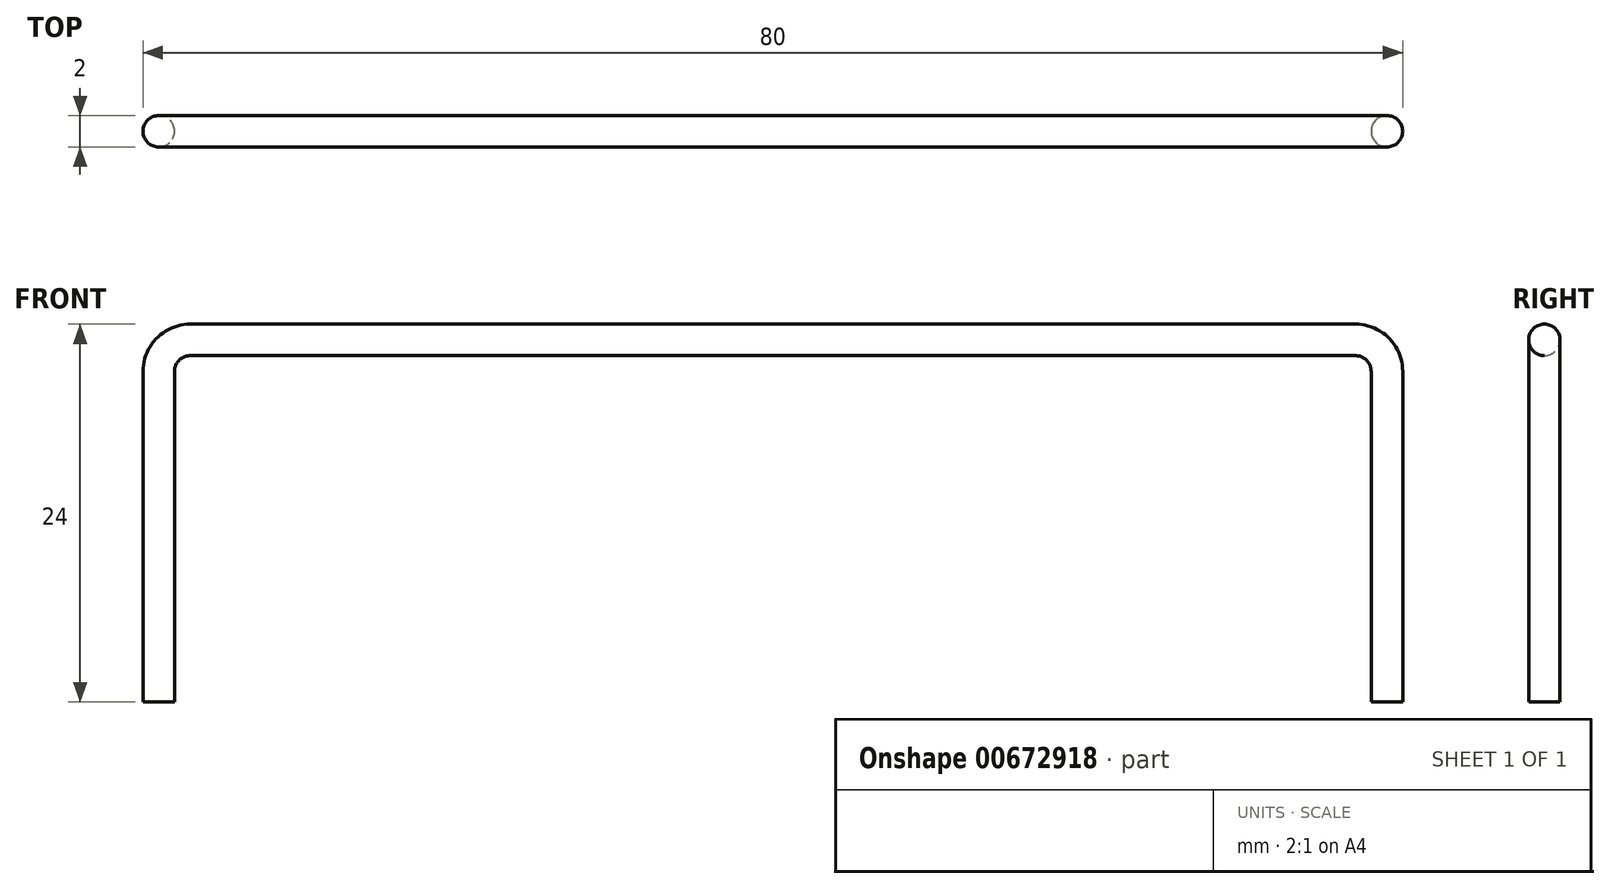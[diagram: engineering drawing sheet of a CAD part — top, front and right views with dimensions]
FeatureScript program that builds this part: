
annotation { "Feature Type Name" : "Feature", "Feature Type Description" : "" }
export const myFeature = defineFeature(function(context is Context, id is Id, definition is map)
    precondition{}
    {
        {
            var Q0;
            Q0=qCreatedBy(makeId("Top.planeOp"),FACE);
            var sketch = newSketch(context, id + "F0", { "sketchPlane" : qUnion([Q0])});
            skCircle(sketch, "E0", {"center": v(-39, 0) * mm, "radius": 1 * mm});
            skCircle(sketch, "E1.MirrorC", {"center": v(39, 0) * mm, "radius": 1 * mm});
            skSolve(sketch);
        }
        {
            var Q0;
            Q0=qCreatedBy(makeId("Front.planeOp"),FACE);
            var sketch = newSketch(context, id + "F1", { "sketchPlane" : qUnion([Q0])});
            skLineSegment(sketch, "E2", {"start": v(-39, 0) * mm, "end": v(-39, 21) * mm});
            skLineSegment(sketch, "E3", {"start": v(-37, 23) * mm, "end": v(0, 23) * mm});
            skPoint(sketch, "E4.visualSharp", {"position": v(-39, 23) * mm});
            skArc(sketch, "E4.filletArc", {"start": v(-37, 23) * mm, "mid": v(-38.41, 22.41) * mm, "end": v(-39, 21) * mm});
            skLineSegment(sketch, "E5.MirrorCS", {"start": v(37, 23) * mm, "end": v(0, 23) * mm});
            skArc(sketch, "E6.MirrorCS", {"start": v(37, 23) * mm, "mid": v(38.41, 22.41) * mm, "end": v(39, 21) * mm});
            skLineSegment(sketch, "E7.MirrorCS", {"start": v(39, 0) * mm, "end": v(39, 21) * mm});
            skSolve(sketch);
        }
        {
            var Q0;
            Q0=makeQuery(id+"F0.imprint","IMPRINT",FACE,{"disambiguationData":[TD([[makeQuery(id+"F0.imprint","IMPRINT",EDGE,{"derivedFrom":sQuery(id+"F0.wireOp",EDGE,"E0")}),1.0]])]});
            var Q1;
            Q1=sQuery(id+"F1.wireOp",EDGE,"E2");
            var Q2;
            Q2=sQuery(id+"F1.wireOp",EDGE,"E4.filletArc");
            var Q3;
            Q3=sQuery(id+"F1.wireOp",EDGE,"E3");
            var Q4;
            Q4=sQuery(id+"F1.wireOp",EDGE,"E5.MirrorCS");
            var Q5;
            Q5=sQuery(id+"F1.wireOp",EDGE,"E6.MirrorCS");
            var Q6;
            Q6=sQuery(id+"F1.wireOp",EDGE,"E7.MirrorCS");
            sweep(context, id + "F2", {"profiles" : qUnion([Q0]), "path" : qUnion([Q1, Q2, Q3, Q4, Q5, Q6])});
        }
    });
